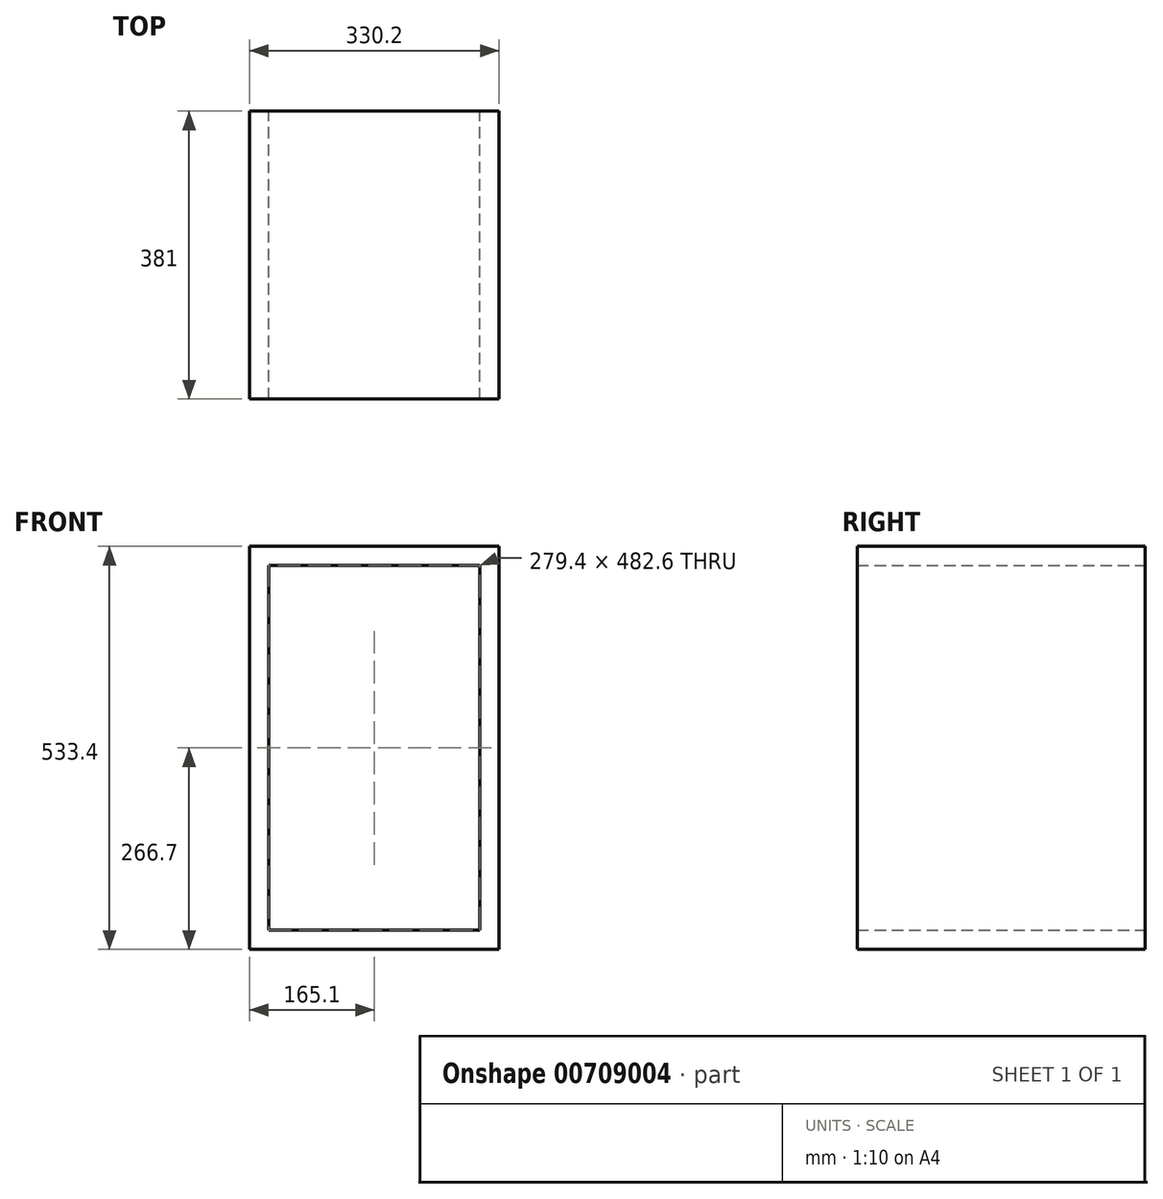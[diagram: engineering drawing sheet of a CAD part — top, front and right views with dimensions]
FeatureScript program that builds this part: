
annotation { "Feature Type Name" : "Feature", "Feature Type Description" : "" }
export const myFeature = defineFeature(function(context is Context, id is Id, definition is map)
    precondition{}
    {
        {
            var Q0;
            Q0=qCreatedBy(makeId("Front.planeOp"),FACE);
            var sketch = newSketch(context, id + "F0", { "sketchPlane" : qUnion([Q0])});
            skLineSegment(sketch, "E0.bottom", {"start": v(-139.7, 241.3) * mm, "end": v(139.7, 241.3) * mm});
            skLineSegment(sketch, "E0.top", {"start": v(-139.7, -241.3) * mm, "end": v(139.7, -241.3) * mm});
            skLineSegment(sketch, "E0.left", {"start": v(-139.7, 241.3) * mm, "end": v(-139.7, -241.3) * mm});
            skLineSegment(sketch, "E0.right", {"start": v(139.7, 241.3) * mm, "end": v(139.7, -241.3) * mm});
            skPoint(sketch, "E0.middle", {"position": v(0, 0) * mm});
            skLineSegment(sketch, "E1.bottom", {"start": v(-165.1, 266.7) * mm, "end": v(165.1, 266.7) * mm});
            skLineSegment(sketch, "E1.top", {"start": v(-165.1, -266.7) * mm, "end": v(165.1, -266.7) * mm});
            skLineSegment(sketch, "E1.left", {"start": v(-165.1, 266.7) * mm, "end": v(-165.1, -266.7) * mm});
            skLineSegment(sketch, "E1.right", {"start": v(165.1, 266.7) * mm, "end": v(165.1, -266.7) * mm});
            skSolve(sketch);
        }
        {
            var Q0;
            Q0=makeQuery(id+"F0.imprint","IMPRINT",FACE,{"disambiguationData":[TD([[makeQuery(id+"F0.imprint","IMPRINT",EDGE,{"derivedFrom":sQuery(id+"F0.wireOp",EDGE,"E0.bottom")}),1.0]])]});
            extrude(context, id + "F1", {"entities" : qUnion([Q0]), "depth" : 381 * mm, "offsetDistance" : 25.4 * mm});
        }
    });
